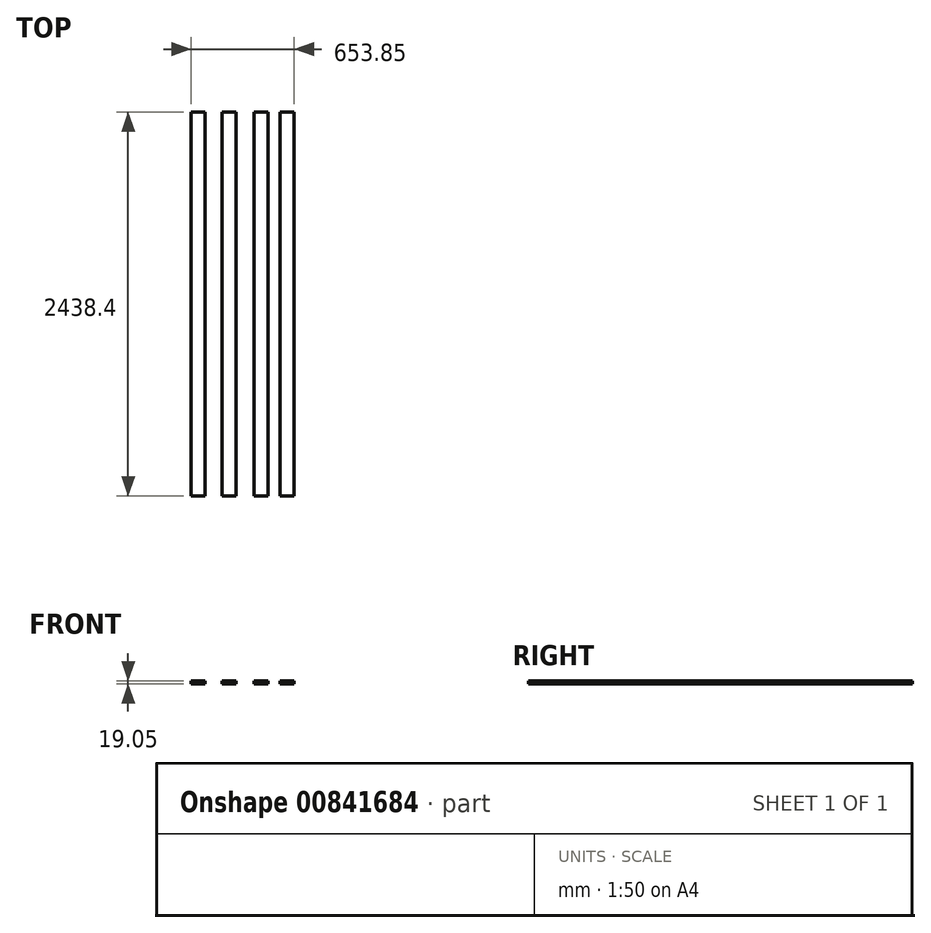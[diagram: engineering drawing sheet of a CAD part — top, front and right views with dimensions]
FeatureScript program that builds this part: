
annotation { "Feature Type Name" : "Feature", "Feature Type Description" : "" }
export const myFeature = defineFeature(function(context is Context, id is Id, definition is map)
    precondition{}
    {
        {
            var Q0;
            Q0=qCreatedBy(makeId("Front.planeOp"),FACE);
            var sketch = newSketch(context, id + "F0", { "sketchPlane" : qUnion([Q0])});
            skLineSegment(sketch, "E0.bottom", {"start": v(-142.95, 0) * mm, "end": v(-54.05, 0) * mm});
            skLineSegment(sketch, "E0.top", {"start": v(-142.95, -19.05) * mm, "end": v(-54.05, -19.05) * mm});
            skLineSegment(sketch, "E0.left", {"start": v(-142.95, 0) * mm, "end": v(-142.95, -19.05) * mm});
            skLineSegment(sketch, "E0.right", {"start": v(-54.05, 0) * mm, "end": v(-54.05, -19.05) * mm});
            skLineSegment(sketch, "E1.bottom", {"start": v(58.11, 0) * mm, "end": v(147.01, 0) * mm});
            skLineSegment(sketch, "E1.top", {"start": v(58.11, -19.05) * mm, "end": v(147.01, -19.05) * mm});
            skLineSegment(sketch, "E1.left", {"start": v(58.11, 0) * mm, "end": v(58.11, -19.05) * mm});
            skLineSegment(sketch, "E1.right", {"start": v(147.01, 0) * mm, "end": v(147.01, -19.05) * mm});
            skLineSegment(sketch, "E2.bottom", {"start": v(-250.78, 0) * mm, "end": v(-339.68, 0) * mm});
            skLineSegment(sketch, "E2.top", {"start": v(-250.78, -19.05) * mm, "end": v(-339.68, -19.05) * mm});
            skLineSegment(sketch, "E2.left", {"start": v(-250.78, 0) * mm, "end": v(-250.78, -19.05) * mm});
            skLineSegment(sketch, "E2.right", {"start": v(-339.68, 0) * mm, "end": v(-339.68, -19.05) * mm});
            skPoint(sketch, "E3.oppositeSnap0", {"position": v(-295.23, -19.05) * mm});
            skLineSegment(sketch, "E3.bottom", {"start": v(225.27, 0) * mm, "end": v(314.17, 0) * mm});
            skLineSegment(sketch, "E3.top", {"start": v(225.27, -19.05) * mm, "end": v(314.17, -19.05) * mm});
            skLineSegment(sketch, "E3.left", {"start": v(225.27, 0) * mm, "end": v(225.27, -19.05) * mm});
            skLineSegment(sketch, "E3.right", {"start": v(314.17, 0) * mm, "end": v(314.17, -19.05) * mm});
            skSolve(sketch);
        }
        {
            var Q0;
            Q0 = qSketchRegion(id + "F0", true);
            extrude(context, id + "F1", {"entities" : qUnion([Q0]), "depth" : 2438.4 * mm, "offsetDistance" : 25.4 * mm});
        }
    });
